# Revit family: Valve-Electronic_Control-Cla_Val-131_01-Flanged--
name_source: partatom
category: Pipe Accessories
units: mm (PartAtom-declared; Revit-internal decimal feet)

## family parameters
Always vertical = Yes
Cut with Voids When Loaded = No
Part Type = Valve - Breaks Into
Round Connector Dimension = Use Diameter
Shared = No
Work Plane-Based = No

## types (1)
- ERROR_LOAD TYPE CATALOG
    Actuator Rod Radius = 0' - 0 5/32"
    Arrow Height = 0' - 1 9/16"
    Arrow Length = 0' - 2 11/32"
    Assembly Code = D2090
    Axis to Arrow = 0' - 7 1/32"
    Body Material = Metal - CLA-VAL - Blue
    Bypass System Offset = 0' - 0 3/4"
    Clearance Horizontal Offset = 0' - 11"
    Clearance Vertical Offset = 1' - 3"
    Connection Axis to Cover Top = 0' - 5 3/4"
    Connection Axis to Side Ports = 0' - 1 11/16"
    Connection Axis to Upper Cover Flange = 0' - 3 1/16"
    Connection Axis to Valve Top = 0' - 6 1/2"
    Connection Size = 2"
    Connection Type = Flanged
    Connection to Connection = 0' - 9 3/8"
    Control Tube Line Radius = 0"
    Control Tube Line Size = 0"
    Cover Lower Flange Diameter = 0' - 6 3/8"
    Cover Lower Flange Thickness = 0' - 0 1/8"
    Cover Top Diameter = 0' - 1 9/32"
    Cover Top Radius = 0' - 0 5/8"
    Cover Upper Flange Diameter = 0' - 6 5/8"
    Cover Upper Flange Radius = 0' - 3 5/16"
    Cover Upper Flange Thickness = 0' - 0 3/4"
    Cv Coefficient = 206
    Default Elevation = 0' - 0"
    Description = Pressure Control Valve
    ENGworks Global = http://www.ENGworksGlobal.com
    Flange Inside Diameter = 0' - 2"
    Flange Outside Radius = 0' - 3"
    Flange Thickness = 0' - 0 21/32"
    Flow Configuration = In/Out
    K Coefficient = 0.384561
    K Coefficient Table = Globe Valve Flanged
    Loss Method = K Coefficient
    Manufacturer = Cla-Val
    Maximum Flow Rate = 125 GPM
    Maximum Flow Rate Value = 125
    Maximum Operating Temperature = 180 °F
    Maximum Working Pressure = 250.00 psi
    Minimum Flow Rate = 0 GPM
    Minimum Flow Rate Value = 0
    Minimum Operating Temperature = -40 °F
    Model = 131-01
    Port Cross Length = 0' - 3 11/32"
    Port Cross Width = 0' - 1 1/8"
    Product Page URL = https://www.cla-val.com
    Series = Waterworks
    Side Port Outside Diameter = 0' - 1 11/32"
    Side Ports Horizontal Offset = 0' - 2 3/16"
    Standards = ASTM A536
    Tick Size = 0' - 5 13/32"
    Top Port Center Offset = 0' - 1 3/32"
    Top Port Vertical Offset = 0' - 1 1/16"
    URL = https://www.cla-val.com
    Unit Weight = 35.00 lb
    Unit Weight Value = 35
    Valve Body Bottom Offset = 0' - 1 1/2"
    Valve Body Bottom Radius = 0' - 1 1/2"
    Valve Body Center Diameter = 0' - 3 3/4"
    Valve Body Tangent Offset = 0' - 0 9/32"
    Valve Body Tangent Radius = 0' - 1 13/16"
    Valve Line Diameter = 0' - 3"
    Valve Line Radius = 0' - 1 1/2"
    Version = 1

## geometry (parser evidence)
native form markers: Sweep x4
no freeform markers — native parametric forms only
